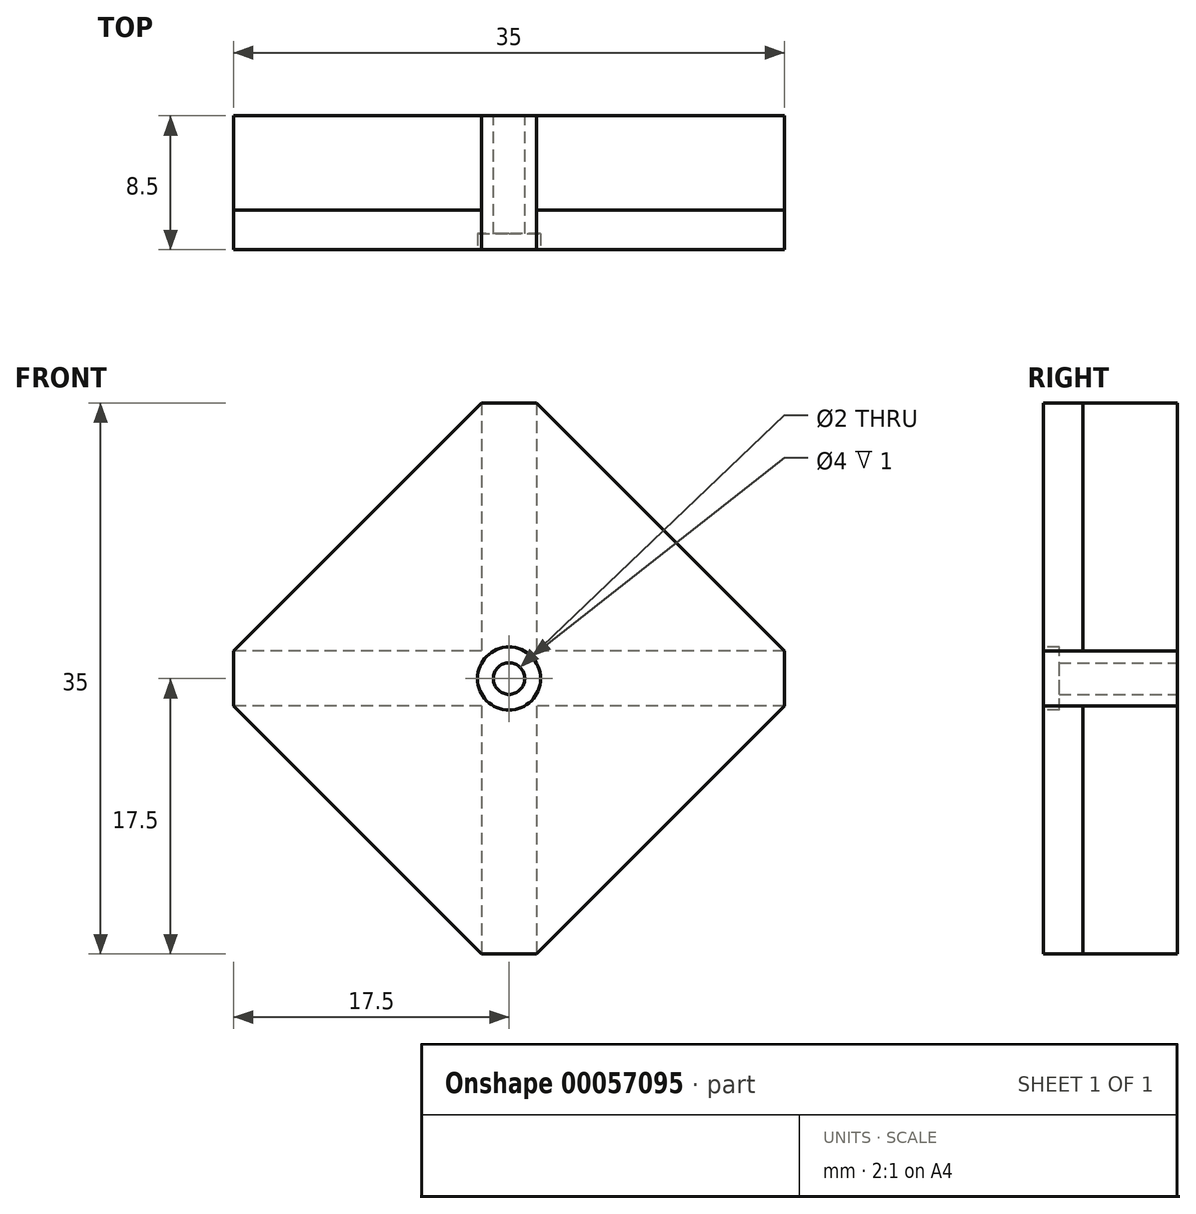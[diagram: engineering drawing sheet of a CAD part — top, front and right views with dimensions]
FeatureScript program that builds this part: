
annotation { "Feature Type Name" : "Feature", "Feature Type Description" : "" }
export const myFeature = defineFeature(function(context is Context, id is Id, definition is map)
    precondition{}
    {
        {
            var Q0;
            Q0=qCreatedBy(makeId("Front.planeOp"),FACE);
            var sketch = newSketch(context, id + "F0", { "sketchPlane" : qUnion([Q0])});
            skLineSegment(sketch, "E0.rect.bottom", {"start": v(1.75, 17.5) * mm, "end": v(-1.75, 17.5) * mm});
            skLineSegment(sketch, "E0.rect.top", {"start": v(1.75, -17.5) * mm, "end": v(-1.75, -17.5) * mm});
            skLineSegment(sketch, "E0.rect.left", {"start": v(1.75, 17.5) * mm, "end": v(1.75, 1.75) * mm});
            skLineSegment(sketch, "E0.rect.right", {"start": v(-1.75, 17.5) * mm, "end": v(-1.75, 1.75) * mm});
            skPoint(sketch, "E0.rect.middle", {"position": v(0, 0) * mm});
            skLineSegment(sketch, "E1.rect.bottom", {"start": v(17.5, 1.75) * mm, "end": v(1.75, 1.75) * mm});
            skLineSegment(sketch, "E1.rect.top", {"start": v(17.5, -1.75) * mm, "end": v(1.75, -1.75) * mm});
            skLineSegment(sketch, "E1.rect.left", {"start": v(17.5, 1.75) * mm, "end": v(17.5, -1.75) * mm});
            skLineSegment(sketch, "E1.rect.right", {"start": v(-17.5, 1.75) * mm, "end": v(-17.5, -1.75) * mm});
            skLineSegment(sketch, "E2.trimOffspring", {"start": v(-1.75, -1.75) * mm, "end": v(-1.75, -17.5) * mm});
            skLineSegment(sketch, "E3.trimOffspring", {"start": v(-1.75, -1.75) * mm, "end": v(-17.5, -1.75) * mm});
            skLineSegment(sketch, "E4.trimOffspring", {"start": v(1.75, -1.75) * mm, "end": v(1.75, -17.5) * mm});
            skLineSegment(sketch, "E5.trimOffspring", {"start": v(-1.75, 1.75) * mm, "end": v(-17.5, 1.75) * mm});
            skSolve(sketch);
        }
        {
            var Q0;
            Q0 = qSketchRegion(id + "F0", true);
            extrude(context, id + "F1", {"entities" : qUnion([Q0]), "depth" : 6 * mm});
        }
        {
            var Q0;
            Q0=makeQuery(id+"F1.opExtrude","CAP_FACE",FACE,{"disambiguationData":[OSD([sQuery(id+"F0.wireOp",EDGE,"E0.rect.bottom"),sQuery(id+"F0.wireOp",EDGE,"E0.rect.top"),sQuery(id+"F0.wireOp",EDGE,"E0.rect.left"),sQuery(id+"F0.wireOp",EDGE,"E0.rect.right"),sQuery(id+"F0.wireOp",EDGE,"E1.rect.bottom"),sQuery(id+"F0.wireOp",EDGE,"E1.rect.top"),sQuery(id+"F0.wireOp",EDGE,"E1.rect.left"),sQuery(id+"F0.wireOp",EDGE,"E1.rect.right"),sQuery(id+"F0.wireOp",EDGE,"E2.trimOffspring"),sQuery(id+"F0.wireOp",EDGE,"E3.trimOffspring"),sQuery(id+"F0.wireOp",EDGE,"E4.trimOffspring"),sQuery(id+"F0.wireOp",EDGE,"E5.trimOffspring")])],"isStart":false});
            var sketch = newSketch(context, id + "F2", { "sketchPlane" : qUnion([Q0])});
            skLineSegment(sketch, "E6", {"start": v(-17.5, 1.75) * mm, "end": v(-1.75, 17.5) * mm});
            skLineSegment(sketch, "E7", {"start": v(-1.75, 17.5) * mm, "end": v(0, 17.5) * mm});
            skLineSegment(sketch, "E8", {"start": v(-17.5, 1.75) * mm, "end": v(-17.5, 0) * mm});
            skLineSegment(sketch, "E9.MirrorCS", {"start": v(17.5, 1.75) * mm, "end": v(17.5, 0) * mm});
            skLineSegment(sketch, "E10.MirrorCS", {"start": v(17.5, 1.75) * mm, "end": v(1.75, 17.5) * mm});
            skLineSegment(sketch, "E11.MirrorCS", {"start": v(1.75, 17.5) * mm, "end": v(0, 17.5) * mm});
            skLineSegment(sketch, "E12.MirrorCS", {"start": v(1.75, -17.5) * mm, "end": v(0, -17.5) * mm});
            skLineSegment(sketch, "E13.MirrorCS", {"start": v(-1.75, -17.5) * mm, "end": v(0, -17.5) * mm});
            skLineSegment(sketch, "E14.MirrorCS", {"start": v(17.5, -1.75) * mm, "end": v(17.5, 0) * mm});
            skLineSegment(sketch, "E15.MirrorCS", {"start": v(-17.5, -1.75) * mm, "end": v(-17.5, 0) * mm});
            skLineSegment(sketch, "E16.MirrorCS", {"start": v(17.5, -1.75) * mm, "end": v(1.75, -17.5) * mm});
            skLineSegment(sketch, "E17.MirrorCS", {"start": v(-17.5, -1.75) * mm, "end": v(-1.75, -17.5) * mm});
            skSolve(sketch);
        }
        {
            var Q0;
            Q0 = qSketchRegion(id + "F2", true);
            extrude(context, id + "F3", {"entities" : qUnion([Q0]), "operationType" : NewBodyOperationType.ADD, "depth" : 2.5 * mm});
        }
        {
            var Q0;
            Q0=makeQuery(id+"F1.opExtrude","CAP_FACE",FACE,{"disambiguationData":[OSD([sQuery(id+"F0.wireOp",EDGE,"E0.rect.bottom"),sQuery(id+"F0.wireOp",EDGE,"E0.rect.top"),sQuery(id+"F0.wireOp",EDGE,"E0.rect.left"),sQuery(id+"F0.wireOp",EDGE,"E0.rect.right"),sQuery(id+"F0.wireOp",EDGE,"E1.rect.bottom"),sQuery(id+"F0.wireOp",EDGE,"E1.rect.top"),sQuery(id+"F0.wireOp",EDGE,"E1.rect.left"),sQuery(id+"F0.wireOp",EDGE,"E1.rect.right"),sQuery(id+"F0.wireOp",EDGE,"E2.trimOffspring"),sQuery(id+"F0.wireOp",EDGE,"E3.trimOffspring"),sQuery(id+"F0.wireOp",EDGE,"E4.trimOffspring"),sQuery(id+"F0.wireOp",EDGE,"E5.trimOffspring")])],"isStart":true});
            var sketch = newSketch(context, id + "F4", { "sketchPlane" : qUnion([Q0])});
            skCircle(sketch, "E18", {"center": v(0, 0) * mm, "radius": 1 * mm});
            skSolve(sketch);
        }
        {
            var Q0;
            Q0 = qSketchRegion(id + "F4", true);
            extrude(context, id + "F5", {"entities" : qUnion([Q0]), "operationType" : NewBodyOperationType.REMOVE, "endBound" : BoundingType.THROUGH_ALL, "oppositeDirection" : true, "depth" : 25 * mm});
        }
        {
            var Q0;
            Q0=makeQuery(id+"F3.opExtrude","CAP_FACE",FACE,{"disambiguationData":[OSD([sQuery(id+"F2.wireOp",EDGE,"E6"),sQuery(id+"F2.wireOp",EDGE,"E7"),sQuery(id+"F2.wireOp",EDGE,"E8"),sQuery(id+"F2.wireOp",EDGE,"E9.MirrorCS"),sQuery(id+"F2.wireOp",EDGE,"E10.MirrorCS"),sQuery(id+"F2.wireOp",EDGE,"E11.MirrorCS"),sQuery(id+"F2.wireOp",EDGE,"E12.MirrorCS"),sQuery(id+"F2.wireOp",EDGE,"E13.MirrorCS"),sQuery(id+"F2.wireOp",EDGE,"E14.MirrorCS"),sQuery(id+"F2.wireOp",EDGE,"E15.MirrorCS"),sQuery(id+"F2.wireOp",EDGE,"E16.MirrorCS"),sQuery(id+"F2.wireOp",EDGE,"E17.MirrorCS")])],"isStart":false});
            var sketch = newSketch(context, id + "F6", { "sketchPlane" : qUnion([Q0])});
            skCircle(sketch, "E19", {"center": v(0, 0) * mm, "radius": 2 * mm});
            skSolve(sketch);
        }
        {
            var Q0;
            Q0 = qSketchRegion(id + "F6", true);
            extrude(context, id + "F7", {"entities" : qUnion([Q0]), "operationType" : NewBodyOperationType.REMOVE, "oppositeDirection" : true, "depth" : 1 * mm});
        }
    });
